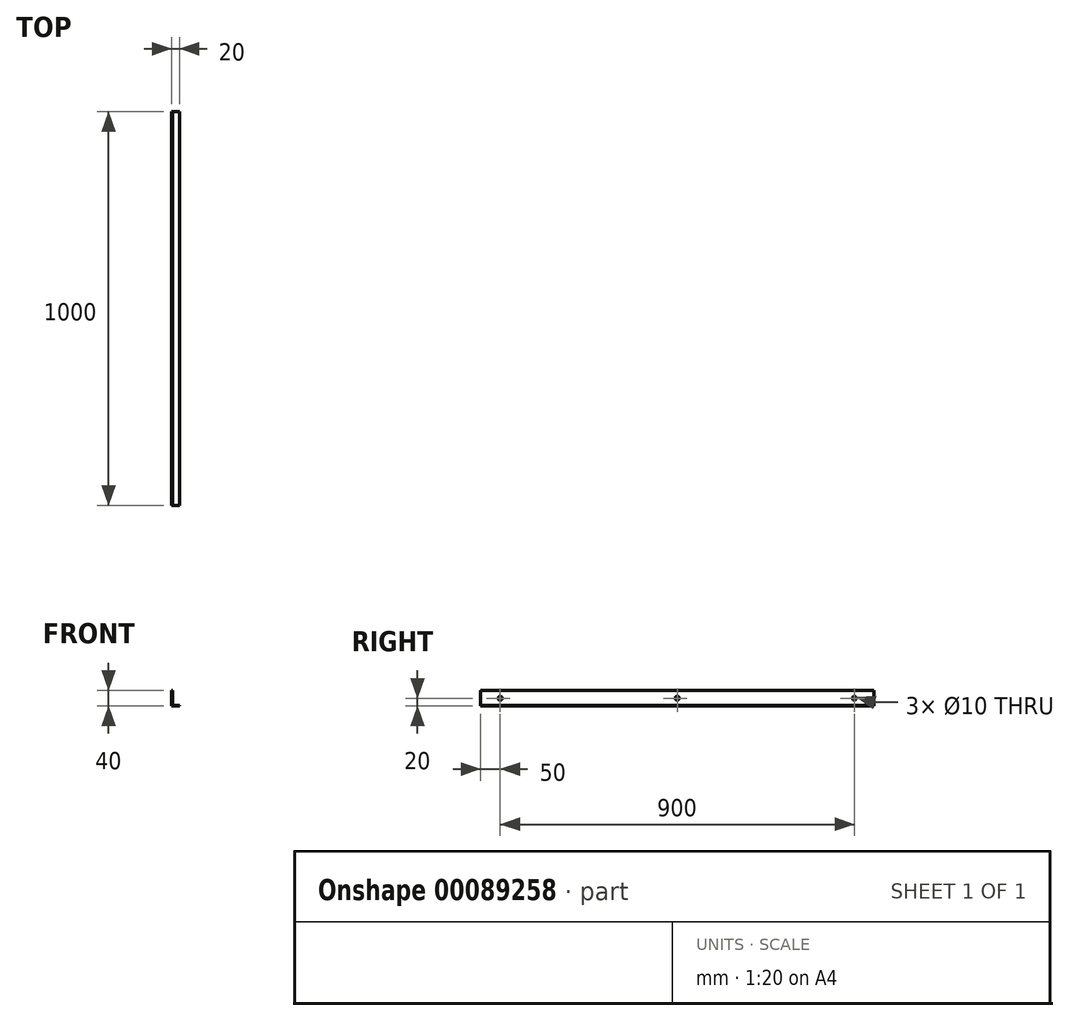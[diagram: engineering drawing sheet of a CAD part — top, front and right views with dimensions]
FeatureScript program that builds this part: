
annotation { "Feature Type Name" : "Feature", "Feature Type Description" : "" }
export const myFeature = defineFeature(function(context is Context, id is Id, definition is map)
    precondition{}
    {
        {
            var Q0;
            Q0=qCreatedBy(makeId("Front.planeOp"),FACE);
            var sketch = newSketch(context, id + "F0", { "sketchPlane" : qUnion([Q0])});
            skLineSegment(sketch, "E0.bottom", {"start": v(-8, 1) * mm, "end": v(10, 1) * mm});
            skLineSegment(sketch, "E0.top", {"start": v(-10, -1) * mm, "end": v(10, -1) * mm});
            skLineSegment(sketch, "E0.left", {"start": v(-10, 1) * mm, "end": v(-10, -1) * mm});
            skLineSegment(sketch, "E0.right", {"start": v(10, 1) * mm, "end": v(10, -1) * mm});
            skPoint(sketch, "E0.middle", {"position": v(0, 0) * mm});
            skLineSegment(sketch, "E1.bottom", {"start": v(-10, -1) * mm, "end": v(-8, -1) * mm});
            skLineSegment(sketch, "E1.top", {"start": v(-10, 39) * mm, "end": v(-8, 39) * mm});
            skLineSegment(sketch, "E1.left", {"start": v(-10, -1) * mm, "end": v(-10, 39) * mm});
            skLineSegment(sketch, "E1.right", {"start": v(-8, 1) * mm, "end": v(-8, 39) * mm});
            skSolve(sketch);
        }
        {
            var Q0;
            Q0=qSketchRegion(id+"F0",true);
            extrude(context, id + "F1", {"entities" : qUnion([Q0]), "depth" : 1000 * mm});
        }
        {
            var Q0;
            Q0=makeQuery(id+"F1.opExtrude","SWEPT_FACE",FACE,{"disambiguationData":[OSD([sQuery(id+"F0.wireOp",EDGE,"E1.left")])]});
            var sketch = newSketch(context, id + "F2", { "sketchPlane" : qUnion([Q0])});
            skLineSegment(sketch, "E2", {"start": v(0, 19) * mm, "end": v(50, 19) * mm, "construction": true});
            skCircle(sketch, "E3", {"center": v(50, 19) * mm, "radius": 5 * mm});
            skLineSegment(sketch, "E4", {"start": v(1000, 19) * mm, "end": v(950, 19) * mm, "construction": true});
            skCircle(sketch, "E5", {"center": v(950, 19) * mm, "radius": 5 * mm});
            skLineSegment(sketch, "E6", {"start": v(50, 19) * mm, "end": v(950, 19) * mm, "construction": true});
            skCircle(sketch, "E7", {"center": v(500, 19) * mm, "radius": 5 * mm});
            skSolve(sketch);
        }
        {
            var Q0;
            Q0=makeQuery(id+"F2.imprint","IMPRINT",FACE,{"disambiguationData":[TD([[makeQuery(id+"F2.imprint","IMPRINT",EDGE,{"derivedFrom":sQuery(id+"F2.wireOp",EDGE,"E3")}),1.0]])]});
            var Q1;
            Q1=makeQuery(id+"F2.imprint","IMPRINT",FACE,{"disambiguationData":[TD([[makeQuery(id+"F2.imprint","IMPRINT",EDGE,{"derivedFrom":sQuery(id+"F2.wireOp",EDGE,"E5")}),1.0]])]});
            var Q2;
            Q2=makeQuery(id+"F2.imprint","IMPRINT",FACE,{"disambiguationData":[TD([[makeQuery(id+"F2.imprint","IMPRINT",EDGE,{"derivedFrom":sQuery(id+"F2.wireOp",EDGE,"E7")}),1.0]])]});
            var Q3;
            Q3=makeQuery(id+"F2.imprint","IMPRINT",FACE,{"disambiguationData":[TD([[makeQuery(id+"F2.imprint","IMPRINT",EDGE,{"derivedFrom":sQuery(id+"F2.wireOp",EDGE,"E7")}),1.0]])]});
            extrude(context, id + "F3", {"entities" : qUnion([Q0, Q1, Q2, Q3]), "operationType" : NewBodyOperationType.REMOVE, "oppositeDirection" : true, "depth" : 25 * mm});
        }
    });
